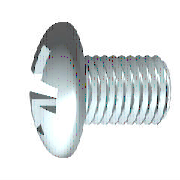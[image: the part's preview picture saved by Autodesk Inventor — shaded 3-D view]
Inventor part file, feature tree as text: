
AUTODESK INVENTOR PART (.ipt)
format: ipt  version: 2022 (Build 260153000, 153)  size: 280,576 bytes
history: native  units: mm (DEFAULTED — no unit token found)
features: other x2, plane x2, extrude x1
ambient origin geometry x7: Origin, YZ Plane, XZ Plane, X Axis, Y Axis, Z Axis, Center Point
bodies: Solid1 (feature_tree)
feature tree (5):
  other  "Базовый элемент"
  plane  "Work Plane1"
  extrude  "Паз"  Depth=4.0mm
  other  "Вырез"
  plane  "Work Plane3"
